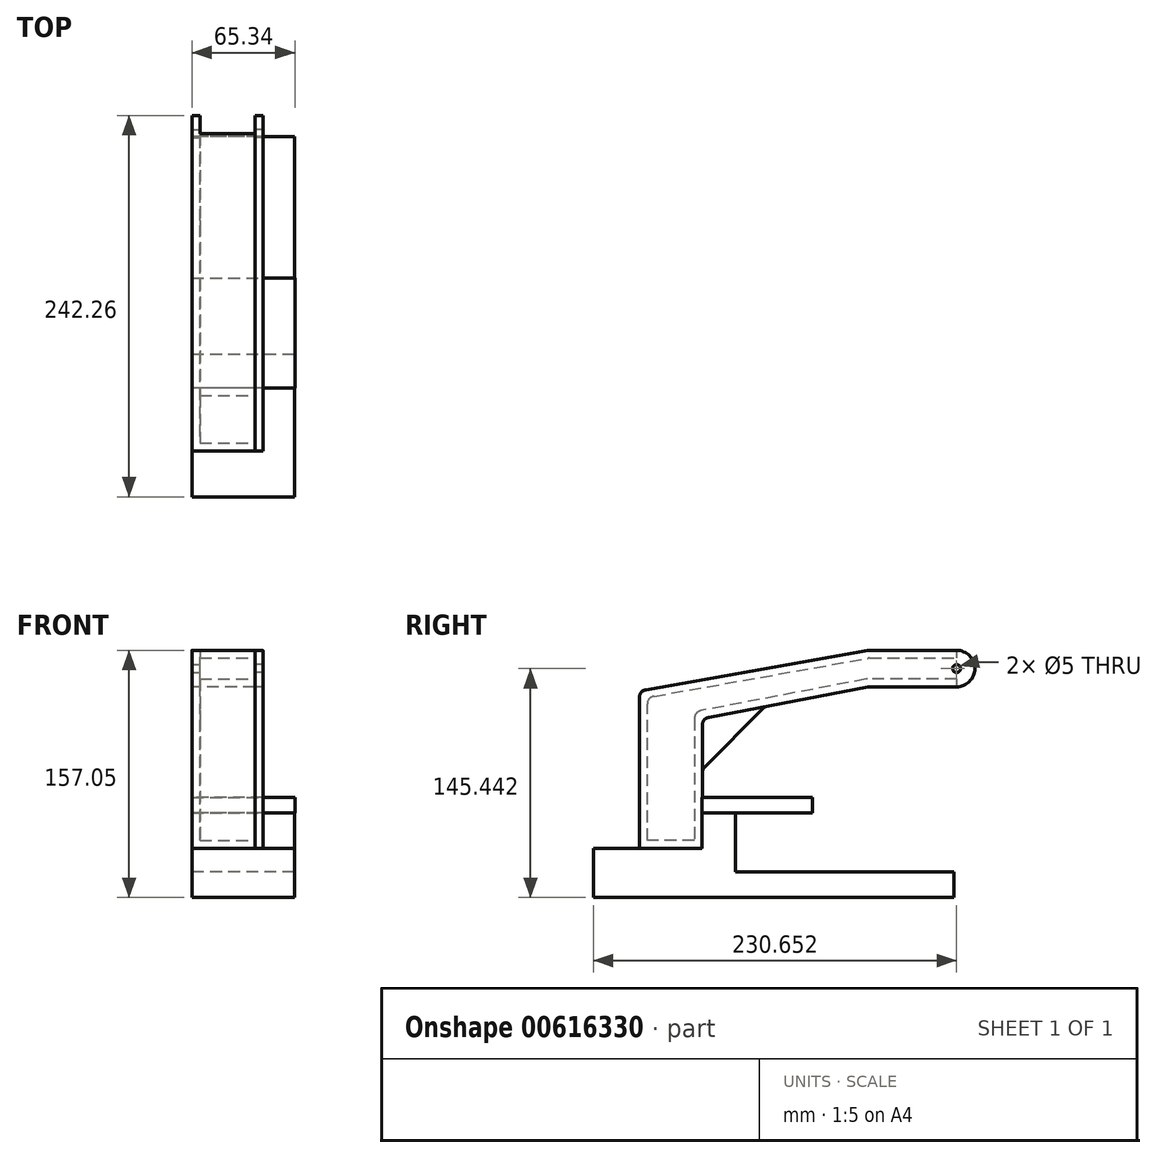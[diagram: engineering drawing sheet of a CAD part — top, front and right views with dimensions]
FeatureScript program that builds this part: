
annotation { "Feature Type Name" : "Feature", "Feature Type Description" : "" }
export const myFeature = defineFeature(function(context is Context, id is Id, definition is map)
    precondition{}
    {
        {
            var Q0;
            Q0=qCreatedBy(makeId("Right.planeOp"),FACE);
            var sketch = newSketch(context, id + "F0", { "sketchPlane" : qUnion([Q0])});
            skLineSegment(sketch, "E0.bottom", {"start": v(20, -50) * mm, "end": v(-20, -50) * mm});
            skLineSegment(sketch, "E0.left", {"start": v(20, -50) * mm, "end": v(20, -2.07) * mm});
            skLineSegment(sketch, "E0.right", {"start": v(-20, -50) * mm, "end": v(-20, 45.8) * mm});
            skPoint(sketch, "E0.middle", {"position": v(0, 0) * mm});
            skLineSegment(sketch, "E1", {"start": v(-15.87, 50.73) * mm, "end": v(124.84, 75.7) * mm});
            skLineSegment(sketch, "E2", {"start": v(61.5, 40.4) * mm, "end": v(124.8, 52.49) * mm});
            skLineSegment(sketch, "E3", {"start": v(125.74, 52.58) * mm, "end": v(181.46, 52.58) * mm});
            skLineSegment(sketch, "E4", {"start": v(181.46, 75.79) * mm, "end": v(125.7, 75.79) * mm});
            skPoint(sketch, "E5.orphan", {"position": v(20, 50) * mm});
            skArc(sketch, "E6", {"start": v(181.46, 75.79) * mm, "mid": v(193.07, 64.18) * mm, "end": v(181.46, 52.58) * mm});
            skPoint(sketch, "E7.visualSharp", {"position": v(-20, 50) * mm});
            skArc(sketch, "E7.filletArc", {"start": v(-15.87, 50.73) * mm, "mid": v(-18.83, 49.02) * mm, "end": v(-20, 45.8) * mm});
            skPoint(sketch, "E8.visualSharp", {"position": v(20, 32.48) * mm});
            skPoint(sketch, "E9.visualSharp", {"position": v(125.27, 75.79) * mm});
            skArc(sketch, "E9.filletArc", {"start": v(125.7, 75.79) * mm, "mid": v(125.27, 75.77) * mm, "end": v(124.84, 75.7) * mm});
            skPoint(sketch, "E10.visualSharp", {"position": v(125.27, 52.58) * mm});
            skArc(sketch, "E10.filletArc", {"start": v(125.74, 52.58) * mm, "mid": v(125.27, 52.56) * mm, "end": v(124.8, 52.49) * mm});
            skLineSegment(sketch, "E11", {"start": v(-15, -45) * mm, "end": v(15, -45) * mm});
            skLineSegment(sketch, "E12", {"start": v(15, -45) * mm, "end": v(15, 0) * mm});
            skLineSegment(sketch, "E13", {"start": v(59.05, 45.03) * mm, "end": v(124.33, 57.49) * mm});
            skLineSegment(sketch, "E14", {"start": v(125.27, 57.58) * mm, "end": v(181.46, 57.58) * mm});
            skLineSegment(sketch, "E15", {"start": v(126.21, 70.79) * mm, "end": v(181.46, 70.79) * mm});
            skArc(sketch, "E16", {"start": v(181.46, 57.58) * mm, "mid": v(188.07, 64.18) * mm, "end": v(181.46, 70.79) * mm});
            skPoint(sketch, "E17.visualSharp", {"position": v(-15, 42.26) * mm});
            skPoint(sketch, "E18.visualSharp", {"position": v(15, 36.62) * mm});
            skArc(sketch, "E19.filletArc", {"start": v(126.21, 70.79) * mm, "mid": v(125.71, 70.76) * mm, "end": v(125.22, 70.69) * mm});
            skPoint(sketch, "E20.visualSharp", {"position": v(124.8, 57.58) * mm});
            skArc(sketch, "E20.filletArc", {"start": v(125.27, 57.58) * mm, "mid": v(124.8, 57.56) * mm, "end": v(124.33, 57.49) * mm});
            skLineSegment(sketch, "E21.0", {"start": v(-10.87, 46.54) * mm, "end": v(125.7, 70.79) * mm});
            skLineSegment(sketch, "E22", {"start": v(-15, -45) * mm, "end": v(-15, 41.62) * mm});
            skArc(sketch, "E23.filletArc", {"start": v(-10.87, 46.54) * mm, "mid": v(-13.83, 44.83) * mm, "end": v(-15, 41.62) * mm});
            skLineSegment(sketch, "E24", {"start": v(21.46, 1.46) * mm, "end": v(58.9, 39.02) * mm});
            skLineSegment(sketch, "E25", {"start": v(56.45, 43.65) * mm, "end": v(16.46, 3.53) * mm});
            skPoint(sketch, "E26.visualSharp", {"position": v(59.99, 40.12) * mm});
            skArc(sketch, "E26.filletArc", {"start": v(61.5, 40.4) * mm, "mid": v(60.1, 39.91) * mm, "end": v(58.9, 39.02) * mm});
            skPoint(sketch, "E27.visualSharp", {"position": v(57.53, 44.74) * mm});
            skArc(sketch, "E27.filletArc", {"start": v(59.05, 45.03) * mm, "mid": v(57.64, 44.53) * mm, "end": v(56.45, 43.65) * mm});
            skPoint(sketch, "E28.visualSharp", {"position": v(20, 0) * mm});
            skArc(sketch, "E28.filletArc", {"start": v(21.46, 1.46) * mm, "mid": v(20.38, -0.16) * mm, "end": v(20, -2.07) * mm});
            skPoint(sketch, "E29.visualSharp", {"position": v(15, 2.07) * mm});
            skArc(sketch, "E29.filletArc", {"start": v(16.46, 3.53) * mm, "mid": v(15.38, 1.9) * mm, "end": v(15, 0) * mm});
            skSolve(sketch);
        }
        {
            var Q0;
            Q0=makeQuery(id+"F0.imprint","IMPRINT",FACE,{"disambiguationData":[TD([[makeQuery(id+"F0.imprint","IMPRINT",EDGE,{"derivedFrom":sQuery(id+"F0.wireOp",EDGE,"E0.bottom")}),-1.0]])]});
            extrude(context, id + "F1", {"entities" : qUnion([Q0]), "depth" : 40 * mm, "offsetDistance" : 25 * mm});
        }
        {
            var Q0;
            Q0=makeQuery(id+"F1.opExtrude","CAP_FACE",FACE,{"disambiguationData":[OSD([sQuery(id+"F0.wireOp",EDGE,"E0.bottom"),sQuery(id+"F0.wireOp",EDGE,"E0.left"),sQuery(id+"F0.wireOp",EDGE,"E0.right"),sQuery(id+"F0.wireOp",EDGE,"E1"),sQuery(id+"F0.wireOp",EDGE,"E2"),sQuery(id+"F0.wireOp",EDGE,"E3"),sQuery(id+"F0.wireOp",EDGE,"E4"),sQuery(id+"F0.wireOp",EDGE,"E6"),sQuery(id+"F0.wireOp",EDGE,"E7.filletArc"),sQuery(id+"F0.wireOp",EDGE,"E8.filletArc"),sQuery(id+"F0.wireOp",EDGE,"E9.filletArc"),sQuery(id+"F0.wireOp",EDGE,"E10.filletArc")])],"isStart":false});
            var sketch = newSketch(context, id + "F2", { "sketchPlane" : qUnion([Q0])});
            skLineSegment(sketch, "E30", {"start": v(-10.87, 46.54) * mm, "end": v(125.28, 70.7) * mm});
            skLineSegment(sketch, "E31", {"start": v(126.15, 70.79) * mm, "end": v(181.46, 70.79) * mm});
            skLineSegment(sketch, "E32", {"start": v(181.65, 57.58) * mm, "end": v(125, 57.58) * mm});
            skLineSegment(sketch, "E33", {"start": v(124.06, 57.49) * mm, "end": v(19.06, 37.44) * mm});
            skLineSegment(sketch, "E34", {"start": v(15, 32.53) * mm, "end": v(15, -45) * mm});
            skArc(sketch, "E35", {"start": v(181.46, 70.79) * mm, "mid": v(188.07, 64.18) * mm, "end": v(181.46, 57.58) * mm});
            skPoint(sketch, "E36.visualSharp", {"position": v(-15, 45.8) * mm});
            skPoint(sketch, "E37.visualSharp", {"position": v(15, 36.67) * mm});
            skArc(sketch, "E37.filletArc", {"start": v(19.06, 37.44) * mm, "mid": v(16.15, 35.72) * mm, "end": v(15, 32.53) * mm});
            skPoint(sketch, "E38.visualSharp", {"position": v(125.7, 70.79) * mm});
            skArc(sketch, "E38.filletArc", {"start": v(126.15, 70.79) * mm, "mid": v(125.71, 70.77) * mm, "end": v(125.28, 70.7) * mm});
            skPoint(sketch, "E39.visualSharp", {"position": v(124.53, 57.58) * mm});
            skArc(sketch, "E39.filletArc", {"start": v(125, 57.58) * mm, "mid": v(124.53, 57.56) * mm, "end": v(124.06, 57.49) * mm});
            skLineSegment(sketch, "E40.0", {"start": v(15, -45) * mm, "end": v(-14.94, -45) * mm});
            skLineSegment(sketch, "E41", {"start": v(-14.94, -45) * mm, "end": v(-15, 41.62) * mm});
            skArc(sketch, "E42.filletArc", {"start": v(-10.87, 46.54) * mm, "mid": v(-13.83, 44.83) * mm, "end": v(-15, 41.62) * mm});
            skLineSegment(sketch, "E43", {"start": v(21.46, 1.46) * mm, "end": v(58.9, 39.02) * mm});
            skSolve(sketch);
        }
        {
            var Q0;
            Q0 = qSketchRegion(id + "F2", true);
            extrude(context, id + "F3", {"entities" : qUnion([Q0]), "operationType" : NewBodyOperationType.REMOVE, "oppositeDirection" : true, "depth" : 35 * mm, "offsetDistance" : 25 * mm});
        }
        {
            var Q0;
            Q0=makeQuery(id+"F1.opExtrude","CAP_FACE",FACE,{"disambiguationData":[OSD([sQuery(id+"F0.wireOp",EDGE,"E0.bottom"),sQuery(id+"F0.wireOp",EDGE,"E0.left"),sQuery(id+"F0.wireOp",EDGE,"E0.right"),sQuery(id+"F0.wireOp",EDGE,"E1"),sQuery(id+"F0.wireOp",EDGE,"E2"),sQuery(id+"F0.wireOp",EDGE,"E3"),sQuery(id+"F0.wireOp",EDGE,"E4"),sQuery(id+"F0.wireOp",EDGE,"E6"),sQuery(id+"F0.wireOp",EDGE,"E7.filletArc"),sQuery(id+"F0.wireOp",EDGE,"E8.filletArc"),sQuery(id+"F0.wireOp",EDGE,"E9.filletArc"),sQuery(id+"F0.wireOp",EDGE,"E10.filletArc")])],"isStart":false});
            var sketch = newSketch(context, id + "F4", { "sketchPlane" : qUnion([Q0])});
            skArc(sketch, "E44", {"start": v(181.46, 75.79) * mm, "mid": v(193.07, 64.18) * mm, "end": v(181.46, 52.58) * mm});
            skLineSegment(sketch, "E45", {"start": v(181.46, 75.79) * mm, "end": v(181.46, 52.58) * mm});
            skSolve(sketch);
        }
        {
            var Q0;
            Q0 = qSketchRegion(id + "F4", true);
            extrude(context, id + "F5", {"entities" : qUnion([Q0]), "operationType" : NewBodyOperationType.REMOVE, "oppositeDirection" : true, "depth" : 35 * mm, "offsetDistance" : 25 * mm});
        }
        {
            var Q0;
            Q0=makeQuery(id+"F5.boolean.opBoolean","MERGE",FACE,{"derivedFrom":[makeQuery(id+"F3.boolean.opBoolean","COPY",FACE,{"derivedFrom":makeQuery(id+"F3.opExtrude","CAP_FACE",FACE,{"disambiguationData":[OSD([sQuery(id+"F2.wireOp",EDGE,"E30"),sQuery(id+"F2.wireOp",EDGE,"E31"),sQuery(id+"F2.wireOp",EDGE,"E32"),sQuery(id+"F2.wireOp",EDGE,"E33"),sQuery(id+"F2.wireOp",EDGE,"E34"),sQuery(id+"F2.wireOp",EDGE,"E35"),sQuery(id+"F2.wireOp",EDGE,"E37.filletArc"),sQuery(id+"F2.wireOp",EDGE,"E38.filletArc"),sQuery(id+"F2.wireOp",EDGE,"E39.filletArc"),sQuery(id+"F2.wireOp",EDGE,"E40.0"),sQuery(id+"F2.wireOp",EDGE,"E41"),sQuery(id+"F2.wireOp",EDGE,"E42.filletArc")])],"isStart":false})}),makeQuery(id+"F5.opExtrude","CAP_FACE",FACE,{"disambiguationData":[OSD([sQuery(id+"F4.wireOp",EDGE,"E44"),sQuery(id+"F4.wireOp",EDGE,"E45")])],"isStart":false})]});
            var sketch = newSketch(context, id + "F6", { "sketchPlane" : qUnion([Q0])});
            skCircle(sketch, "E46", {"center": v(181.46, 64.18) * mm, "radius": 2.5 * mm});
            skSolve(sketch);
        }
        {
            var Q0;
            Q0 = qSketchRegion(id + "F6", true);
            extrude(context, id + "F7", {"entities" : qUnion([Q0]), "operationType" : NewBodyOperationType.REMOVE, "endBound" : BoundingType.THROUGH_ALL, "oppositeDirection" : true, "depth" : 25 * mm, "offsetDistance" : 25 * mm});
        }
        {
            var Q0;
            Q0=makeQuery(id+"F1.opExtrude","CAP_FACE",FACE,{"disambiguationData":[OSD([sQuery(id+"F0.wireOp",EDGE,"E0.bottom"),sQuery(id+"F0.wireOp",EDGE,"E0.left"),sQuery(id+"F0.wireOp",EDGE,"E0.right"),sQuery(id+"F0.wireOp",EDGE,"E1"),sQuery(id+"F0.wireOp",EDGE,"E2"),sQuery(id+"F0.wireOp",EDGE,"E3"),sQuery(id+"F0.wireOp",EDGE,"E4"),sQuery(id+"F0.wireOp",EDGE,"E6"),sQuery(id+"F0.wireOp",EDGE,"E7.filletArc"),sQuery(id+"F0.wireOp",EDGE,"E8.filletArc"),sQuery(id+"F0.wireOp",EDGE,"E9.filletArc"),sQuery(id+"F0.wireOp",EDGE,"E10.filletArc")])],"isStart":false});
            var sketch = newSketch(context, id + "F8", { "sketchPlane" : qUnion([Q0])});
            skLineSegment(sketch, "E47", {"start": v(125.28, 52.49) * mm, "end": v(24.06, 33.17) * mm});
            skLineSegment(sketch, "E48", {"start": v(20, 28.26) * mm, "end": v(20, -50) * mm});
            skLineSegment(sketch, "E49", {"start": v(20, -50) * mm, "end": v(-20, -50) * mm});
            skLineSegment(sketch, "E50", {"start": v(181.46, 75.79) * mm, "end": v(126.15, 75.79) * mm});
            skLineSegment(sketch, "E51", {"start": v(125.28, 75.7) * mm, "end": v(-15.87, 50.65) * mm});
            skLineSegment(sketch, "E52", {"start": v(-20, 45.73) * mm, "end": v(-20, -50) * mm});
            skLineSegment(sketch, "E53", {"start": v(126.22, 52.58) * mm, "end": v(181.46, 52.58) * mm});
            skArc(sketch, "E54", {"start": v(181.46, 52.58) * mm, "mid": v(193.07, 64.18) * mm, "end": v(181.46, 75.79) * mm});
            skPoint(sketch, "E55.visualSharp", {"position": v(20, 32.4) * mm});
            skArc(sketch, "E55.filletArc", {"start": v(24.06, 33.17) * mm, "mid": v(21.15, 31.44) * mm, "end": v(20, 28.26) * mm});
            skPoint(sketch, "E56.visualSharp", {"position": v(-20, 49.92) * mm});
            skArc(sketch, "E56.filletArc", {"start": v(-15.87, 50.65) * mm, "mid": v(-18.83, 48.94) * mm, "end": v(-20, 45.73) * mm});
            skPoint(sketch, "E57.visualSharp", {"position": v(125.7, 75.79) * mm});
            skArc(sketch, "E57.filletArc", {"start": v(126.15, 75.79) * mm, "mid": v(125.71, 75.77) * mm, "end": v(125.28, 75.7) * mm});
            skPoint(sketch, "E58.visualSharp", {"position": v(125.74, 52.58) * mm});
            skArc(sketch, "E58.filletArc", {"start": v(126.22, 52.58) * mm, "mid": v(125.74, 52.56) * mm, "end": v(125.28, 52.49) * mm});
            skCircle(sketch, "E59", {"center": v(181.46, 64.18) * mm, "radius": 2.5 * mm});
            skSolve(sketch);
        }
        {
            var Q0;
            Q0 = qSketchRegion(id + "F8", true);
            extrude(context, id + "F9", {"entities" : qUnion([Q0]), "depth" : 5 * mm, "offsetDistance" : 25 * mm});
        }
        {
            var Q0;
            Q0=qCreatedBy(makeId("Right.planeOp"),FACE);
            var sketch = newSketch(context, id + "F10", { "sketchPlane" : qUnion([Q0])});
            skLineSegment(sketch, "E60", {"start": v(19.76, -50) * mm, "end": v(-49.19, -50) * mm});
            skLineSegment(sketch, "E61", {"start": v(19.76, -50) * mm, "end": v(19.76, -27.62) * mm});
            skLineSegment(sketch, "E62", {"start": v(41.12, -27.62) * mm, "end": v(19.76, -27.62) * mm});
            skLineSegment(sketch, "E63", {"start": v(41.12, -27.62) * mm, "end": v(41.12, -64.9) * mm});
            skLineSegment(sketch, "E64", {"start": v(179.74, -64.9) * mm, "end": v(41.12, -64.9) * mm});
            skLineSegment(sketch, "E65", {"start": v(179.74, -64.9) * mm, "end": v(179.74, -81.26) * mm});
            skLineSegment(sketch, "E66", {"start": v(-49.19, -81.26) * mm, "end": v(179.74, -81.26) * mm});
            skLineSegment(sketch, "E67", {"start": v(-49.19, -81.26) * mm, "end": v(-49.19, -50) * mm});
            skSolve(sketch);
        }
        {
            var Q0;
            Q0 = qSketchRegion(id + "F10", true);
            extrude(context, id + "F11", {"entities" : qUnion([Q0]), "depth" : 65 * mm, "offsetDistance" : 25 * mm});
        }
        {
            var Q0;
            Q0=makeQuery(id+"F11.opExtrude","SWEPT_FACE",FACE,{"disambiguationData":[OSD([sQuery(id+"F10.wireOp",EDGE,"E62")])]});
            var sketch = newSketch(context, id + "F12", { "sketchPlane" : qUnion([Q0])});
            skLineSegment(sketch, "E68.bottom", {"start": v(0, 19.76) * mm, "end": v(65.34, 19.76) * mm});
            skLineSegment(sketch, "E68.top", {"start": v(0, 89.8) * mm, "end": v(65.34, 89.8) * mm});
            skLineSegment(sketch, "E68.left", {"start": v(0, 89.8) * mm, "end": v(0, 19.76) * mm});
            skLineSegment(sketch, "E68.right", {"start": v(65.34, 89.8) * mm, "end": v(65.34, 19.76) * mm});
            skSolve(sketch);
        }
        {
            var Q0;
            Q0 = qSketchRegion(id + "F12", true);
            extrude(context, id + "F13", {"entities" : qUnion([Q0]), "depth" : 10 * mm, "offsetDistance" : 25 * mm});
        }
    });
